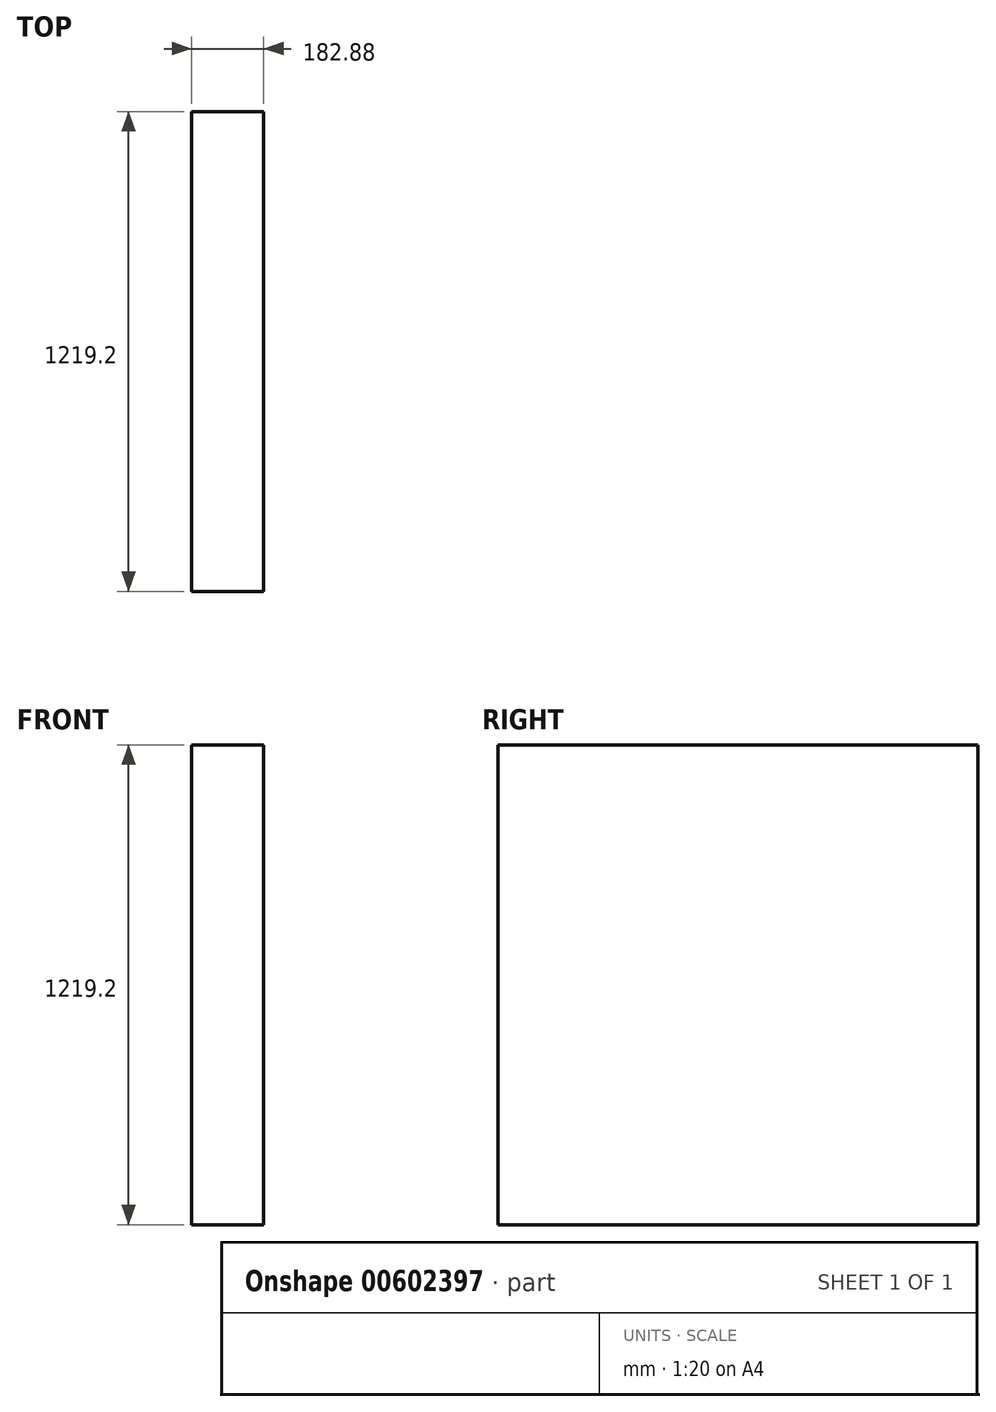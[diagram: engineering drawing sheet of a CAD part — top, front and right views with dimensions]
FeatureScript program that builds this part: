
annotation { "Feature Type Name" : "Feature", "Feature Type Description" : "" }
export const myFeature = defineFeature(function(context is Context, id is Id, definition is map)
    precondition{}
    {
        {
            var Q0;
            Q0=qCreatedBy(makeId("Top.planeOp"),FACE);
            var sketch = newSketch(context, id + "F0", { "sketchPlane" : qUnion([Q0])});
            skLineSegment(sketch, "E0.bottom", {"start": v(0, 0) * mm, "end": v(0, 0) * mm});
            skLineSegment(sketch, "E1.bottom", {"start": v(0, 0) * mm, "end": v(182.88, 0) * mm});
            skLineSegment(sketch, "E1.top", {"start": v(0, -1219.2) * mm, "end": v(182.88, -1219.2) * mm});
            skLineSegment(sketch, "E1.left", {"start": v(0, 0) * mm, "end": v(0, -1219.2) * mm});
            skLineSegment(sketch, "E1.right", {"start": v(182.88, 0) * mm, "end": v(182.88, -1219.2) * mm});
            skSolve(sketch);
        }
        {
            var Q0;
            Q0=makeQuery(id+"F0.imprint","IMPRINT",FACE,{"disambiguationData":[TD([[makeQuery(id+"F0.imprint","IMPRINT",EDGE,{"derivedFrom":sQuery(id+"F0.wireOp",EDGE,"E1.bottom")}),-1.0]])]});
            extrude(context, id + "F1", {"entities" : qUnion([Q0]), "depth" : 1219.2 * mm, "offsetDistance" : 30.48 * mm});
        }
    });
